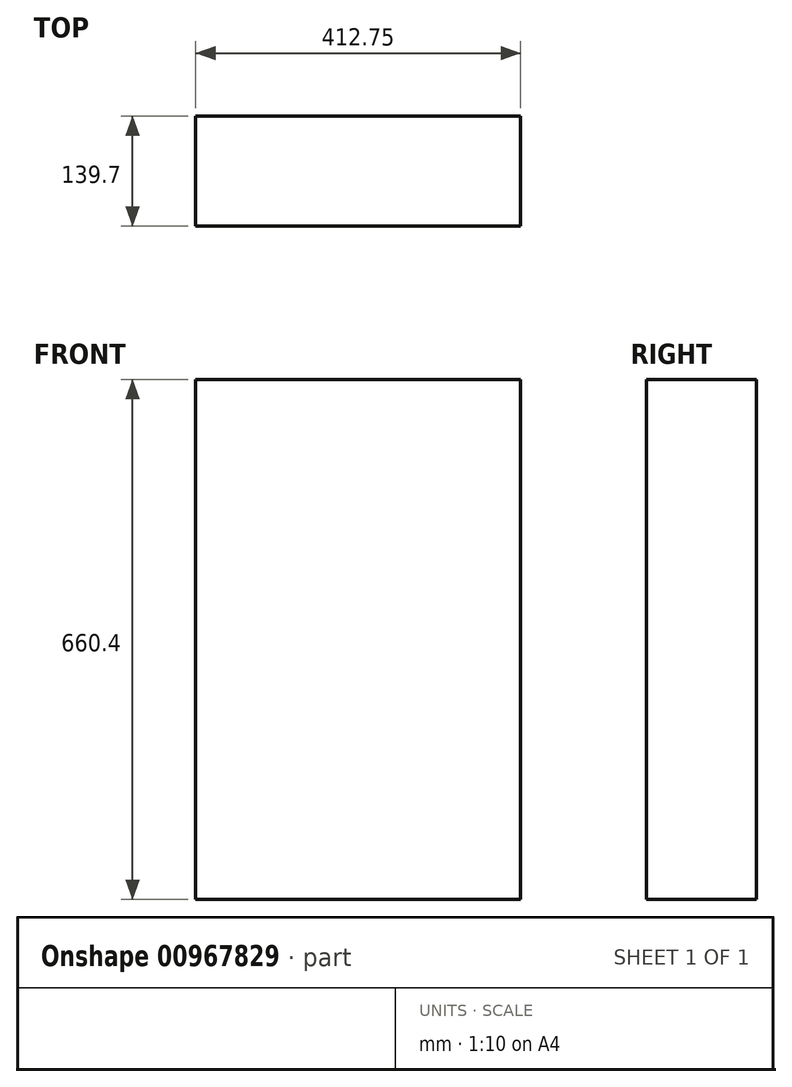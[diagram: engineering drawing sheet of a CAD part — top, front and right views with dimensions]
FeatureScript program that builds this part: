
annotation { "Feature Type Name" : "Feature", "Feature Type Description" : "" }
export const myFeature = defineFeature(function(context is Context, id is Id, definition is map)
    precondition{}
    {
        {
            var Q0;
            Q0=qCreatedBy(makeId("Front.planeOp"),FACE);
            var sketch = newSketch(context, id + "F0", { "sketchPlane" : qUnion([Q0])});
            skLineSegment(sketch, "E0.bottom", {"start": v(-1040.76, 1089.42) * mm, "end": v(1045.78, 1089.42) * mm});
            skLineSegment(sketch, "E0.top", {"start": v(-1040.76, -1342.63) * mm, "end": v(1045.78, -1342.63) * mm});
            skLineSegment(sketch, "E0.left", {"start": v(-1040.76, 1089.42) * mm, "end": v(-1040.76, -1342.63) * mm});
            skLineSegment(sketch, "E0.right", {"start": v(1045.78, 1089.42) * mm, "end": v(1045.78, -1342.63) * mm});
            skLineSegment(sketch, "E1.bottom", {"start": v(-450.2, 1089.42) * mm, "end": v(-37.46, 1089.42) * mm});
            skLineSegment(sketch, "E1.top", {"start": v(-450.2, 429.02) * mm, "end": v(-37.46, 429.02) * mm});
            skLineSegment(sketch, "E1.left", {"start": v(-450.2, 1089.42) * mm, "end": v(-450.2, 429.02) * mm});
            skLineSegment(sketch, "E1.right", {"start": v(-37.46, 1089.42) * mm, "end": v(-37.46, 429.02) * mm});
            skLineSegment(sketch, "E2.top", {"start": v(-450.2, 403.62) * mm, "end": v(-37.46, 403.62) * mm});
            skLineSegment(sketch, "E2.left", {"start": v(-450.2, 429.02) * mm, "end": v(-450.2, 403.62) * mm});
            skLineSegment(sketch, "E2.right", {"start": v(-37.46, 429.02) * mm, "end": v(-37.46, 403.62) * mm});
            skLineSegment(sketch, "E3.bottom", {"start": v(-450.2, 403.62) * mm, "end": v(-399.4, 403.62) * mm});
            skLineSegment(sketch, "E3.top", {"start": v(-450.2, 302.02) * mm, "end": v(-399.4, 302.02) * mm});
            skLineSegment(sketch, "E3.left", {"start": v(-450.2, 403.62) * mm, "end": v(-450.2, 302.02) * mm});
            skLineSegment(sketch, "E3.right", {"start": v(-399.4, 403.62) * mm, "end": v(-399.4, 302.02) * mm});
            skLineSegment(sketch, "E4.bottom", {"start": v(-37.46, 403.62) * mm, "end": v(-88.26, 403.62) * mm});
            skLineSegment(sketch, "E4.top", {"start": v(-37.46, 302.02) * mm, "end": v(-88.26, 302.02) * mm});
            skLineSegment(sketch, "E4.left", {"start": v(-37.46, 403.62) * mm, "end": v(-37.46, 302.02) * mm});
            skLineSegment(sketch, "E4.right", {"start": v(-88.26, 403.62) * mm, "end": v(-88.26, 302.02) * mm});
            skSolve(sketch);
        }
        {
            var Q0;
            Q0=makeQuery(id+"F0.imprint","IMPRINT",FACE,{"disambiguationData":[TD([[makeQuery(id+"F0.imprint","IMPRINT",EDGE,{"derivedFrom":sQuery(id+"F0.wireOp",EDGE,"E1.top")}),1.0]])]});
            extrude(context, id + "F1", {"entities" : qUnion([Q0]), "depth" : 139.7 * mm, "offsetDistance" : 25.4 * mm});
        }
    });
